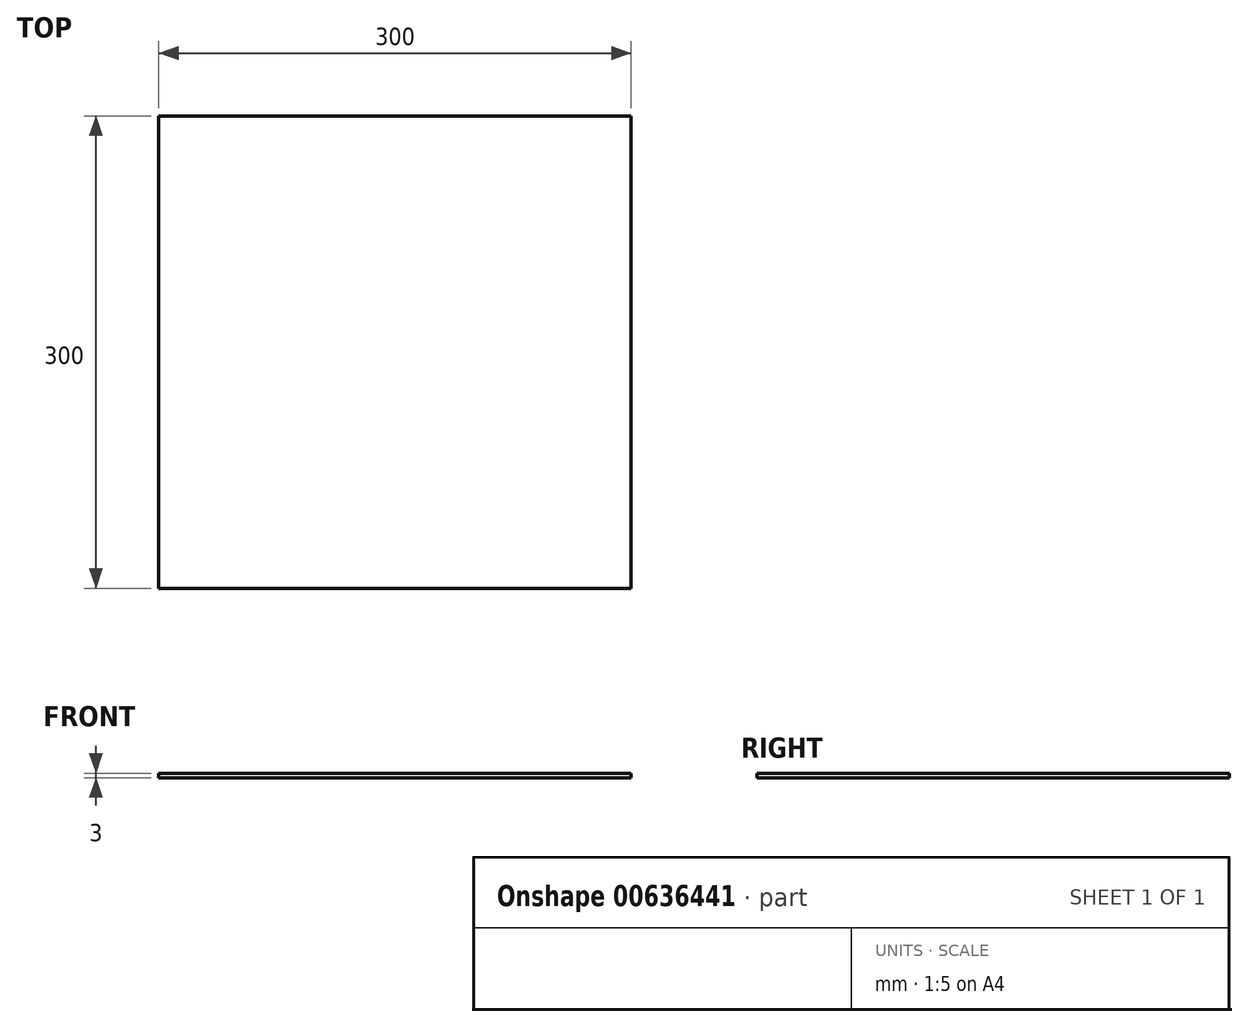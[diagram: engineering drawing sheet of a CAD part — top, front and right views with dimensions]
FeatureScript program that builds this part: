
annotation { "Feature Type Name" : "Feature", "Feature Type Description" : "" }
export const myFeature = defineFeature(function(context is Context, id is Id, definition is map)
    precondition{}
    {
        {
            var Q0;
            Q0=qCreatedBy(makeId("Top.planeOp"),FACE);
            var sketch = newSketch(context, id + "F0", { "sketchPlane" : qUnion([Q0])});
            skLineSegment(sketch, "E0.bottom", {"start": v(0, 0) * mm, "end": v(300, 0) * mm});
            skLineSegment(sketch, "E0.top", {"start": v(0, 300) * mm, "end": v(300, 300) * mm});
            skLineSegment(sketch, "E0.left", {"start": v(0, 0) * mm, "end": v(0, 300) * mm});
            skLineSegment(sketch, "E0.right", {"start": v(300, 0) * mm, "end": v(300, 300) * mm});
            skSolve(sketch);
        }
        {
            var Q0;
            Q0 = qSketchRegion(id + "F0", true);
            extrude(context, id + "F1", {"entities" : qUnion([Q0]), "depth" : 3 * mm, "offsetDistance" : 25 * mm});
        }
    });
